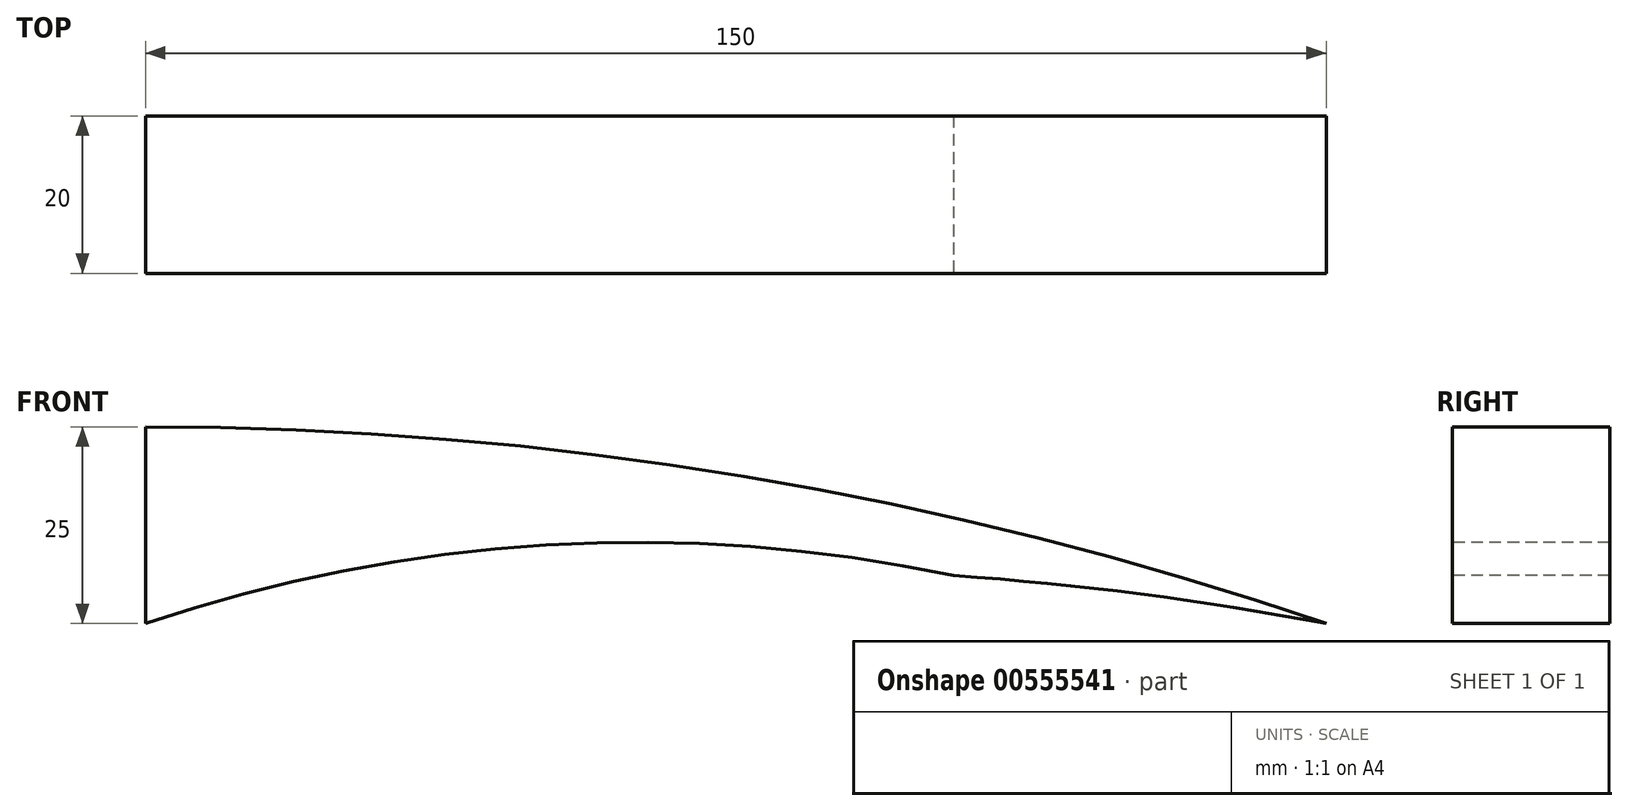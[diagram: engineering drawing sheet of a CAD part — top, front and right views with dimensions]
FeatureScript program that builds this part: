
annotation { "Feature Type Name" : "Feature", "Feature Type Description" : "" }
export const myFeature = defineFeature(function(context is Context, id is Id, definition is map)
    precondition{}
    {
        {
            var Q0;
            Q0=qCreatedBy(makeId("Top.planeOp"),FACE);
            var sketch = newSketch(context, id + "F0", { "sketchPlane" : qUnion([Q0])});
            skLineSegment(sketch, "E0.bottom", {"start": v(-72.36, -1.2) * mm, "end": v(77.64, -1.2) * mm});
            skLineSegment(sketch, "E0.top", {"start": v(-72.36, -21.2) * mm, "end": v(77.64, -21.2) * mm});
            skLineSegment(sketch, "E0.left", {"start": v(-72.36, -1.2) * mm, "end": v(-72.36, -21.2) * mm});
            skLineSegment(sketch, "E0.right", {"start": v(77.64, -1.2) * mm, "end": v(77.64, -21.2) * mm});
            skSolve(sketch);
        }
        {
            var Q0;
            Q0=makeQuery(id+"F0.imprint","IMPRINT",FACE,{"disambiguationData":[TD([[makeQuery(id+"F0.imprint","IMPRINT",EDGE,{"derivedFrom":sQuery(id+"F0.wireOp",EDGE,"E0.bottom")}),-1.0]])]});
            extrude(context, id + "F1", {"entities" : qUnion([Q0]), "depth" : 25 * mm, "offsetDistance" : 25 * mm});
        }
        {
            var Q0;
            Q0=makeQuery(id+"F1.opExtrude","SWEPT_FACE",FACE,{"disambiguationData":[OSD([sQuery(id+"F0.wireOp",EDGE,"E0.top")])]});
            var sketch = newSketch(context, id + "F2", { "sketchPlane" : qUnion([Q0])});
            skArc(sketch, "E1", {"start": v(77.64, 0) * mm, "mid": v(3.67, 18.7) * mm, "end": v(-72.36, 25) * mm});
            skLineSegment(sketch, "E2", {"start": v(-72.36, 25) * mm, "end": v(-72.36, 0) * mm});
            skLineSegment(sketch, "E3", {"start": v(-72.36, 0) * mm, "end": v(77.64, 0) * mm});
            skSolve(sketch);
        }
        {
            var Q0;
            Q0=makeQuery(id+"F2.imprint","IMPRINT",FACE,{"disambiguationData":[TD([[makeQuery(id+"F2.imprint","IMPRINT",EDGE,{"derivedFrom":sQuery(id+"F2.wireOp",EDGE,"E1")}),-1.0]])]});
            extrude(context, id + "F3", {"entities" : qUnion([Q0]), "operationType" : NewBodyOperationType.REMOVE, "endBound" : BoundingType.THROUGH_ALL, "oppositeDirection" : true, "depth" : 25 * mm, "offsetDistance" : 25 * mm});
        }
        {
            var Q0;
            Q0=makeQuery(id+"F1.opExtrude","SWEPT_FACE",FACE,{"disambiguationData":[OSD([sQuery(id+"F0.wireOp",EDGE,"E0.top")])]});
            var sketch = newSketch(context, id + "F4", { "sketchPlane" : qUnion([Q0])});
            skArc(sketch, "E4", {"start": v(77.64, 0) * mm, "mid": v(2.64, 7.05) * mm, "end": v(-72.36, 0) * mm});
            skArc(sketch, "E5", {"start": v(52.44, 0) * mm, "mid": v(-9.96, 10.33) * mm, "end": v(-72.36, 0) * mm});
            skSolve(sketch);
        }
        {
            var Q0;
            {var subQ0=sQuery(id+"F4.wireOp",EDGE,"E5");var subQ1=sQuery(id+"F4.wireOp",EDGE,"E4");var subQ4=makeQuery(id+"F4.imprint","INTERSECT",VERTEX,{"derivedFrom":[subQ1,subQ0]});Q0=makeQuery(id+"F4.imprint","IMPRINT",FACE,{"disambiguationData":[TD([[makeQuery(id+"F4.imprint","IMPRINT",EDGE,{"disambiguationData":[TD([[subQ4,-1.0]])],"derivedFrom":subQ1}),-1.0]])]});}
            var Q1;
            {var subQ1=makeQuery(id+"F1.opExtrude","CAP_EDGE",EDGE,{"disambiguationData":[OSD([sQuery(id+"F0.wireOp",EDGE,"E0.top")])],"isStart":true});var subQ3=sQuery(id+"F4.wireOp",EDGE,"E5");var subQ5=makeQuery(id+"F4.imprint","INTERSECT",VERTEX,{"derivedFrom":[subQ1,subQ3]});Q1=makeQuery(id+"F4.imprint","IMPRINT",FACE,{"disambiguationData":[TD([[makeQuery(id+"F4.imprint","IMPRINT",EDGE,{"disambiguationData":[TD([[subQ5,-1.0]])],"derivedFrom":subQ3}),-1.0]])]});}
            var Q2;
            {var subQ0=sQuery(id+"F4.wireOp",EDGE,"E5");var subQ2=sQuery(id+"F0.wireOp",EDGE,"E0.top");var subQ3=makeQuery(id+"F1.opExtrude","CAP_EDGE",EDGE,{"disambiguationData":[OSD([subQ2])],"isStart":true});var subQ6=makeQuery(id+"F4.imprint","INTERSECT",VERTEX,{"derivedFrom":[subQ3,subQ0]});Q2=makeQuery(id+"F4.imprint","IMPRINT",FACE,{"disambiguationData":[TD([[makeQuery(id+"F4.imprint","IMPRINT",EDGE,{"disambiguationData":[TD([[subQ6,-1.0]])],"derivedFrom":subQ0}),1.0]])]});}
            extrude(context, id + "F5", {"entities" : qUnion([Q0, Q1, Q2]), "operationType" : NewBodyOperationType.REMOVE, "endBound" : BoundingType.THROUGH_ALL, "oppositeDirection" : true, "depth" : 25 * mm, "offsetDistance" : 25 * mm});
        }
    });
